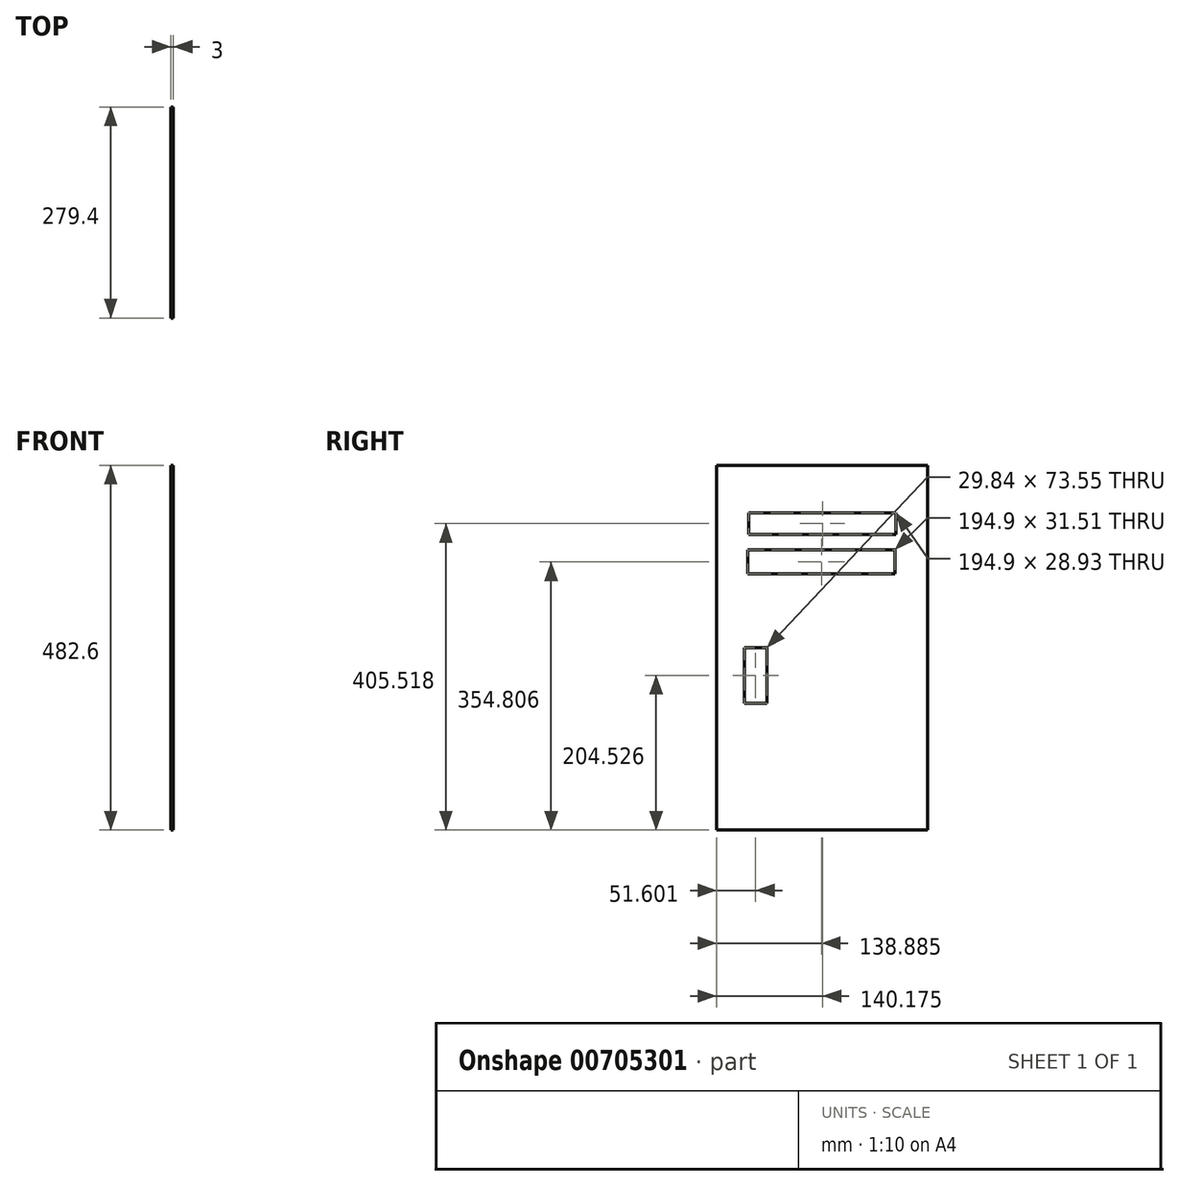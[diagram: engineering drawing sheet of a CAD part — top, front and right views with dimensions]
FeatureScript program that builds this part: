
annotation { "Feature Type Name" : "Feature", "Feature Type Description" : "" }
export const myFeature = defineFeature(function(context is Context, id is Id, definition is map)
    precondition{}
    {
        {
            var Q0;
            Q0=qCreatedBy(makeId("Right.planeOp"),FACE);
            var sketch = newSketch(context, id + "F0", { "sketchPlane" : qUnion([Q0])});
            skLineSegment(sketch, "E0.bottom", {"start": v(-139.7, 241.3) * mm, "end": v(139.7, 241.3) * mm});
            skLineSegment(sketch, "E0.top", {"start": v(-139.7, -241.3) * mm, "end": v(139.7, -241.3) * mm});
            skLineSegment(sketch, "E0.left", {"start": v(-139.7, 241.3) * mm, "end": v(-139.7, -241.3) * mm});
            skLineSegment(sketch, "E0.right", {"start": v(139.7, 241.3) * mm, "end": v(139.7, -241.3) * mm});
            skPoint(sketch, "E0.middle", {"position": v(0, 0) * mm});
            skLineSegment(sketch, "E1.bottom", {"start": v(-96.98, 178.68) * mm, "end": v(97.93, 178.68) * mm});
            skLineSegment(sketch, "E1.top", {"start": v(-96.98, 149.76) * mm, "end": v(97.93, 149.76) * mm});
            skLineSegment(sketch, "E1.left", {"start": v(-96.98, 178.68) * mm, "end": v(-96.98, 149.76) * mm});
            skLineSegment(sketch, "E1.right", {"start": v(97.93, 178.68) * mm, "end": v(97.93, 149.76) * mm});
            skLineSegment(sketch, "E2.bottom", {"start": v(-98.27, 129.26) * mm, "end": v(96.64, 129.26) * mm});
            skLineSegment(sketch, "E2.top", {"start": v(-98.27, 97.75) * mm, "end": v(96.64, 97.75) * mm});
            skLineSegment(sketch, "E2.left", {"start": v(-98.27, 129.26) * mm, "end": v(-98.27, 97.75) * mm});
            skLineSegment(sketch, "E2.right", {"start": v(96.64, 129.26) * mm, "end": v(96.64, 97.75) * mm});
            skLineSegment(sketch, "E3.bottom", {"start": v(-103.02, 0) * mm, "end": v(-73.18, 0) * mm});
            skLineSegment(sketch, "E3.top", {"start": v(-103.02, -73.55) * mm, "end": v(-73.18, -73.55) * mm});
            skLineSegment(sketch, "E3.left", {"start": v(-103.02, 0) * mm, "end": v(-103.02, -73.55) * mm});
            skLineSegment(sketch, "E3.right", {"start": v(-73.18, 0) * mm, "end": v(-73.18, -73.55) * mm});
            skSolve(sketch);
        }
        {
            var Q0;
            Q0 = qSketchRegion(id + "F0", true);
            extrude(context, id + "F1", {"entities" : qUnion([Q0]), "depth" : 3 * mm, "offsetDistance" : 25.4 * mm});
        }
    });
